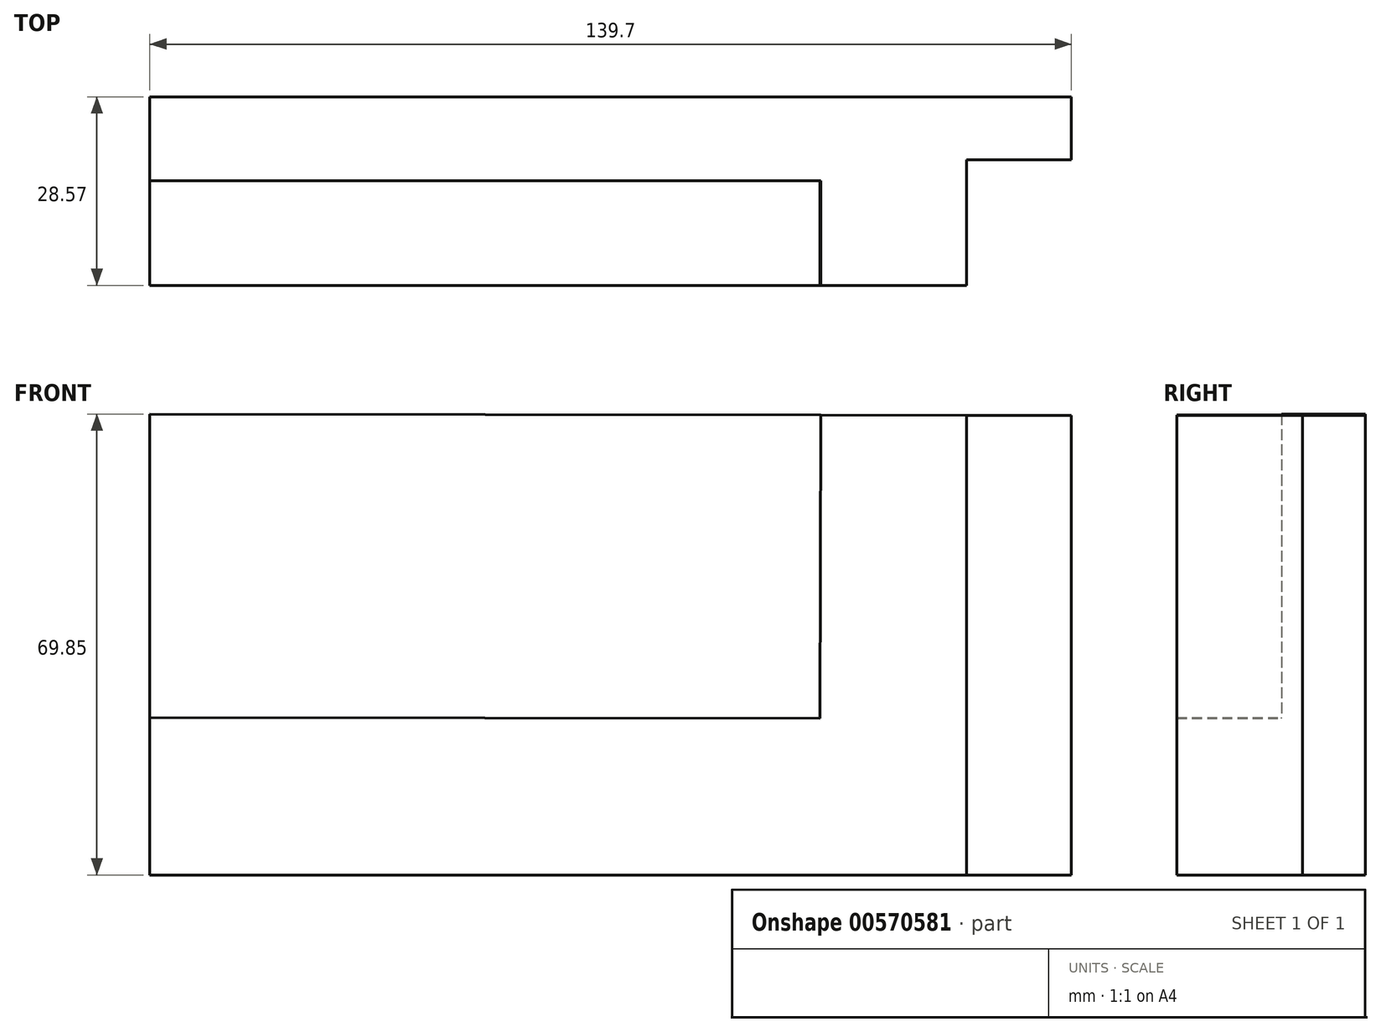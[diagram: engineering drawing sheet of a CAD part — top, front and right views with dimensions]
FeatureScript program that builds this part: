
annotation { "Feature Type Name" : "Feature", "Feature Type Description" : "" }
export const myFeature = defineFeature(function(context is Context, id is Id, definition is map)
    precondition{}
    {
        {
            var Q0;
            Q0=qCreatedBy(makeId("Front.planeOp"),FACE);
            var sketch = newSketch(context, id + "F0", { "sketchPlane" : qUnion([Q0])});
            skLineSegment(sketch, "E0", {"start": v(-82.79, 49.9) * mm, "end": v(-82.79, -19.96) * mm});
            skLineSegment(sketch, "E1", {"start": v(-82.79, -19.96) * mm, "end": v(56.91, -19.96) * mm});
            skLineSegment(sketch, "E2", {"start": v(56.91, -19.96) * mm, "end": v(56.91, 49.66) * mm});
            skLineSegment(sketch, "E3", {"start": v(56.91, 49.66) * mm, "end": v(-82.79, 49.9) * mm});
            skLineSegment(sketch, "E4", {"start": v(18.89, 49.73) * mm, "end": v(18.81, 3.74) * mm});
            skLineSegment(sketch, "E5", {"start": v(18.81, 3.74) * mm, "end": v(-82.79, 3.9) * mm});
            skLineSegment(sketch, "E6", {"start": v(41.04, 49.69) * mm, "end": v(41.04, -19.96) * mm});
            skSolve(sketch);
        }
        {
            var Q0;
            {var subQ0=sQuery(id+"F0.wireOp",EDGE,"E4");Q0=makeQuery(id+"F0.imprint","IMPRINT",FACE,{"disambiguationData":[TD([[makeQuery(id+"F0.imprint","IMPRINT",EDGE,{"derivedFrom":subQ0}),1.0]])]});}
            extrude(context, id + "F1", {"entities" : qUnion([Q0]), "depth" : 28.57 * mm, "offsetDistance" : 25.4 * mm});
        }
        {
            var Q0;
            {var subQ0=sQuery(id+"F0.wireOp",EDGE,"E2");Q0=makeQuery(id+"F0.imprint","IMPRINT",FACE,{"disambiguationData":[TD([[makeQuery(id+"F0.imprint","IMPRINT",EDGE,{"derivedFrom":subQ0}),1.0]])]});}
            extrude(context, id + "F2", {"entities" : qUnion([Q0]), "operationType" : NewBodyOperationType.ADD, "depth" : 9.52 * mm, "offsetDistance" : 25.4 * mm});
        }
        {
            var Q0;
            {var subQ4=sQuery(id+"F0.wireOp",EDGE,"E4");Q0=makeQuery(id+"F0.imprint","IMPRINT",FACE,{"disambiguationData":[TD([[makeQuery(id+"F0.imprint","IMPRINT",EDGE,{"derivedFrom":subQ4}),-1.0]])]});}
            extrude(context, id + "F3", {"entities" : qUnion([Q0]), "operationType" : NewBodyOperationType.ADD, "depth" : 12.7 * mm, "offsetDistance" : 25.4 * mm});
        }
    });
